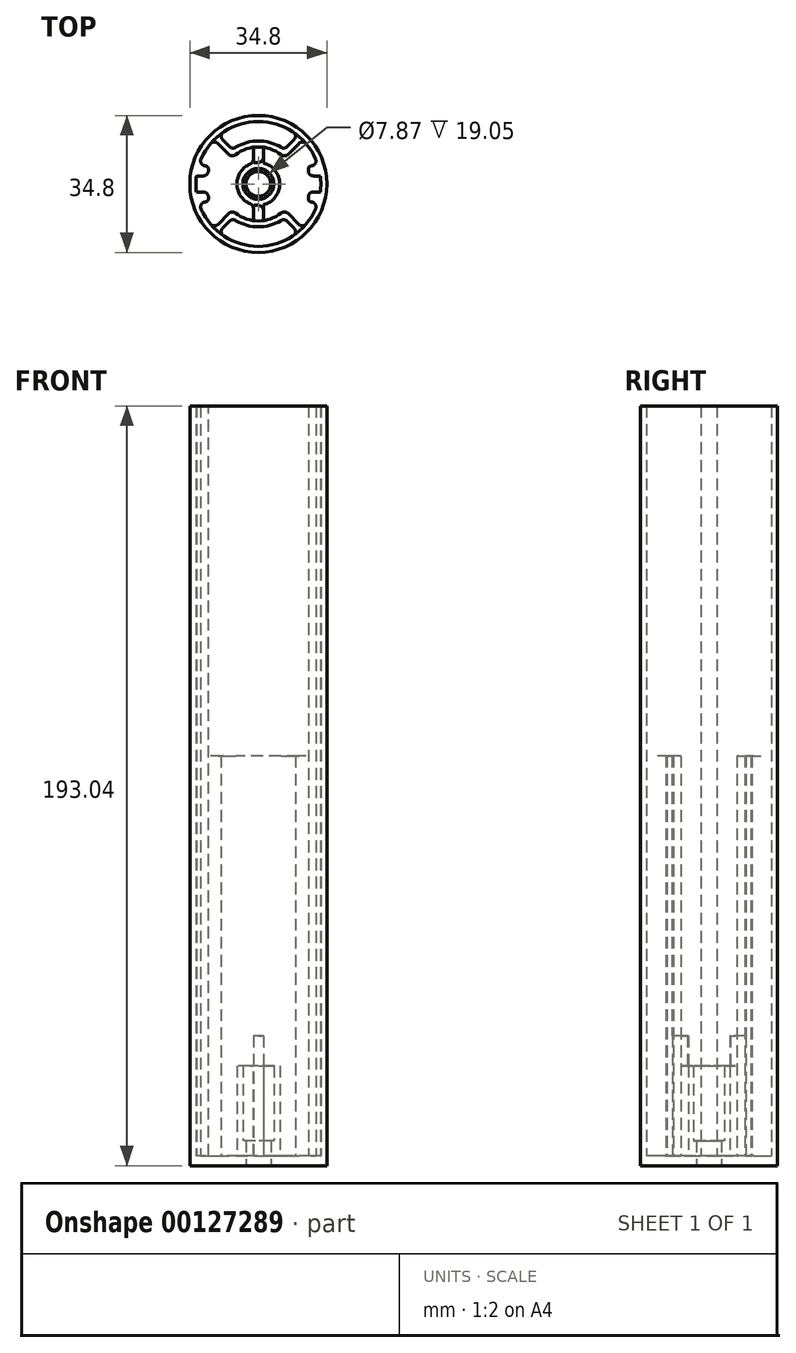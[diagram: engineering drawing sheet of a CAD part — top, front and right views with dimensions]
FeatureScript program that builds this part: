
annotation { "Feature Type Name" : "Feature", "Feature Type Description" : "" }
export const myFeature = defineFeature(function(context is Context, id is Id, definition is map)
    precondition{}
    {
        {
            var Q0;
            Q0=qCreatedBy(makeId("Top.planeOp"),FACE);
            var sketch = newSketch(context, id + "F0", { "sketchPlane" : qUnion([Q0])});
            skCircle(sketch, "E0", {"center": v(0, 0) * mm, "radius": 15.88 * mm, "construction": true});
            skCircle(sketch, "E1", {"center": v(0, 0) * mm, "radius": 17.4 * mm});
            skLineSegment(sketch, "E2", {"start": v(15.88, 0) * mm, "end": v(17.4, 0) * mm, "construction": true});
            skCircle(sketch, "E3", {"center": v(0, 0) * mm, "radius": 3.18 * mm});
            skCircle(sketch, "E4", {"center": v(0, 0) * mm, "radius": 3.94 * mm, "construction": true});
            skCircle(sketch, "E5", {"center": v(0, 0) * mm, "radius": 9.4 * mm, "construction": true});
            skSolve(sketch);
        }
        {
            var Q0;
            Q0 = qSketchRegion(id + "F0", true);
            extrude(context, id + "F1", {"entities" : qUnion([Q0]), "depth" : 2.54 * mm});
        }
        {
            var Q0;
            Q0=makeQuery(id+"F1.opExtrude","CAP_FACE",FACE,{"disambiguationData":[OSD([sQuery(id+"F0.wireOp",EDGE,"E1"),sQuery(id+"F0.wireOp",EDGE,"E3")])],"isStart":false});
            var sketch = newSketch(context, id + "F2", { "sketchPlane" : qUnion([Q0])});
            skCircle(sketch, "E6", {"center": v(0, 0) * mm, "radius": 3.18 * mm});
            skCircle(sketch, "E7", {"center": v(0, 0) * mm, "radius": 5.46 * mm});
            skLineSegment(sketch, "E8", {"start": v(3.94, 0) * mm, "end": v(5.46, 0) * mm});
            skSolve(sketch);
        }
        {
            var Q0;
            Q0 = qSketchRegion(id + "F2", true);
            extrude(context, id + "F3", {"entities" : qUnion([Q0]), "operationType" : NewBodyOperationType.ADD, "depth" : 3.8 * mm});
        }
        {
            var Q0;
            Q0=makeQuery(id+"F3.opExtrude","CAP_FACE",FACE,{"disambiguationData":[OSD([sQuery(id+"F2.wireOp",EDGE,"E6"),sQuery(id+"F2.wireOp",EDGE,"E7")])],"isStart":false});
            var sketch = newSketch(context, id + "F4", { "sketchPlane" : qUnion([Q0])});
            skCircle(sketch, "E9", {"center": v(0, 0) * mm, "radius": 5.46 * mm});
            skCircle(sketch, "E10", {"center": v(0, 0) * mm, "radius": 3.94 * mm});
            skSolve(sketch);
        }
        {
            var Q0;
            Q0 = qSketchRegion(id + "F4", true);
            extrude(context, id + "F5", {"entities" : qUnion([Q0]), "operationType" : NewBodyOperationType.ADD, "depth" : 19.05 * mm});
        }
        {
            var Q0;
            Q0=makeQuery(id+"F1.opExtrude","CAP_FACE",FACE,{"disambiguationData":[OSD([sQuery(id+"F0.wireOp",EDGE,"E1"),sQuery(id+"F0.wireOp",EDGE,"E3")])],"isStart":false});
            var sketch = newSketch(context, id + "F6", { "sketchPlane" : qUnion([Q0])});
            skCircle(sketch, "E11", {"center": v(0, 0) * mm, "radius": 17.4 * mm});
            skLineSegment(sketch, "E12", {"start": v(-11.23, 11.23) * mm, "end": v(-6.65, 6.65) * mm});
            skLineSegment(sketch, "E13", {"start": v(-11.23, -11.23) * mm, "end": v(-6.65, -6.65) * mm});
            skArc(sketch, "E14", {"start": v(-6.65, 6.65) * mm, "mid": v(-9.4, 0) * mm, "end": v(-6.65, -6.65) * mm, "construction": true});
            skArc(sketch, "E15", {"start": v(-6.65, -6.65) * mm, "mid": v(0, -9.4) * mm, "end": v(6.65, -6.65) * mm});
            skArc(sketch, "E16", {"start": v(6.65, -6.65) * mm, "mid": v(9.4, 0) * mm, "end": v(6.65, 6.65) * mm, "construction": true});
            skArc(sketch, "E17", {"start": v(6.65, 6.65) * mm, "mid": v(0, 9.4) * mm, "end": v(-6.65, 6.65) * mm});
            skLineSegment(sketch, "E18", {"start": v(6.65, 6.65) * mm, "end": v(11.23, 11.23) * mm});
            skLineSegment(sketch, "E19", {"start": v(6.65, -6.65) * mm, "end": v(11.23, -11.23) * mm});
            skLineSegment(sketch, "E20", {"start": v(-6.65, -6.65) * mm, "end": v(6.65, 6.65) * mm, "construction": true});
            skLineSegment(sketch, "E21", {"start": v(-6.65, 6.65) * mm, "end": v(6.65, -6.65) * mm, "construction": true});
            skLineSegment(sketch, "E22", {"start": v(-10.1, -12.25) * mm, "end": v(-6.57, -8.72) * mm});
            skLineSegment(sketch, "E23", {"start": v(6.57, -8.72) * mm, "end": v(10.1, -12.25) * mm});
            skArc(sketch, "E24", {"start": v(-6.57, -8.72) * mm, "mid": v(0, -10.92) * mm, "end": v(6.57, -8.72) * mm});
            skArc(sketch, "E25", {"start": v(-10.1, -12.25) * mm, "mid": v(0, -15.87) * mm, "end": v(10.1, -12.25) * mm});
            skArc(sketch, "E26", {"start": v(10.1, -12.25) * mm, "mid": v(10.67, -11.75) * mm, "end": v(11.23, -11.23) * mm, "construction": true});
            skArc(sketch, "E27", {"start": v(-11.23, -11.23) * mm, "mid": v(-10.67, -11.75) * mm, "end": v(-10.1, -12.25) * mm, "construction": true});
            skArc(sketch, "E28", {"start": v(11.23, -11.23) * mm, "mid": v(13.63, -8.15) * mm, "end": v(15.2, -4.57) * mm});
            skLineSegment(sketch, "E29", {"start": v(0, -9.4) * mm, "end": v(0, -10.92) * mm, "construction": true});
            skLineSegment(sketch, "E30", {"start": v(-10.1, 12.25) * mm, "end": v(-6.57, 8.72) * mm});
            skLineSegment(sketch, "E31", {"start": v(10.1, 12.25) * mm, "end": v(6.57, 8.72) * mm});
            skArc(sketch, "E32", {"start": v(6.57, 8.72) * mm, "mid": v(0, 10.92) * mm, "end": v(-6.57, 8.72) * mm});
            skLineSegment(sketch, "E33", {"start": v(0, 9.4) * mm, "end": v(0, 10.92) * mm, "construction": true});
            skArc(sketch, "E34", {"start": v(-11.23, 11.23) * mm, "mid": v(-13.63, 8.15) * mm, "end": v(-15.2, 4.57) * mm});
            skArc(sketch, "E35", {"start": v(-10.1, 12.25) * mm, "mid": v(-10.67, 11.75) * mm, "end": v(-11.23, 11.23) * mm, "construction": true});
            skArc(sketch, "E36", {"start": v(10.1, 12.25) * mm, "mid": v(0, 15.88) * mm, "end": v(-10.1, 12.25) * mm});
            skArc(sketch, "E37", {"start": v(11.23, 11.23) * mm, "mid": v(10.67, 11.75) * mm, "end": v(10.1, 12.25) * mm, "construction": true});
            skArc(sketch, "E38", {"start": v(-15.2, 4.57) * mm, "mid": v(-15.53, 3.31) * mm, "end": v(-15.74, 2.03) * mm, "construction": true});
            skArc(sketch, "E39", {"start": v(-15.74, -2.03) * mm, "mid": v(-15.53, -3.31) * mm, "end": v(-15.2, -4.57) * mm, "construction": true});
            skArc(sketch, "E40", {"start": v(-15.74, 2.03) * mm, "mid": v(-15.88, 0) * mm, "end": v(-15.74, -2.03) * mm});
            skArc(sketch, "E41", {"start": v(-15.2, -4.57) * mm, "mid": v(-13.63, -8.15) * mm, "end": v(-11.23, -11.23) * mm});
            skArc(sketch, "E42", {"start": v(15.2, -4.57) * mm, "mid": v(15.53, -3.31) * mm, "end": v(15.74, -2.03) * mm, "construction": true});
            skArc(sketch, "E43", {"start": v(15.74, -2.03) * mm, "mid": v(15.88, 0) * mm, "end": v(15.74, 2.03) * mm});
            skArc(sketch, "E44", {"start": v(15.74, 2.03) * mm, "mid": v(15.53, 3.31) * mm, "end": v(15.2, 4.57) * mm, "construction": true});
            skArc(sketch, "E45", {"start": v(15.2, 4.57) * mm, "mid": v(13.63, 8.15) * mm, "end": v(11.23, 11.23) * mm});
            skPoint(sketch, "E46", {"position": v(-15.88, 0) * mm});
            skPoint(sketch, "E47", {"position": v(15.88, 0) * mm});
            skLineSegment(sketch, "E48", {"start": v(-15.2, 4.57) * mm, "end": v(-12.7, 4.57) * mm});
            skLineSegment(sketch, "E49", {"start": v(-12.7, 4.57) * mm, "end": v(-12.7, 2.03) * mm});
            skLineSegment(sketch, "E50", {"start": v(-12.7, 2.03) * mm, "end": v(-15.74, 2.03) * mm});
            skLineSegment(sketch, "E51", {"start": v(-15.74, -2.03) * mm, "end": v(-12.7, -2.03) * mm});
            skLineSegment(sketch, "E52", {"start": v(-12.7, -2.03) * mm, "end": v(-12.7, -4.57) * mm});
            skLineSegment(sketch, "E53", {"start": v(-12.7, -4.57) * mm, "end": v(-15.2, -4.57) * mm});
            skLineSegment(sketch, "E54", {"start": v(15.2, 4.57) * mm, "end": v(12.7, 4.57) * mm});
            skLineSegment(sketch, "E55", {"start": v(12.7, 4.57) * mm, "end": v(12.7, 2.03) * mm});
            skLineSegment(sketch, "E56", {"start": v(12.7, 2.03) * mm, "end": v(15.74, 2.03) * mm});
            skLineSegment(sketch, "E57", {"start": v(15.74, -2.03) * mm, "end": v(12.7, -2.03) * mm});
            skLineSegment(sketch, "E58", {"start": v(12.7, -2.03) * mm, "end": v(12.7, -4.57) * mm});
            skLineSegment(sketch, "E59", {"start": v(12.7, -4.57) * mm, "end": v(15.2, -4.57) * mm});
            skSolve(sketch);
        }
        {
            var Q0;
            Q0 = qSketchRegion(id + "F6", true);
            extrude(context, id + "F7", {"entities" : qUnion([Q0]), "operationType" : NewBodyOperationType.ADD, "depth" : 101.6 * mm});
        }
        {
            var Q0;
            Q0=makeQuery(id+"F7.boolean.opBoolean","SPLIT",FACE,{"disambiguationData":[TD([makeQuery(id+"F3.opExtrude","SWEPT_FACE",FACE,{"disambiguationData":[OSD([sQuery(id+"F2.wireOp",EDGE,"E7")])]})])],"derivedFrom":makeQuery(id+"F1.opExtrude","CAP_FACE",FACE,{"disambiguationData":[OSD([sQuery(id+"F0.wireOp",EDGE,"E1"),sQuery(id+"F0.wireOp",EDGE,"E3")])],"isStart":false})});
            var sketch = newSketch(context, id + "F8", { "sketchPlane" : qUnion([Q0])});
            skLineSegment(sketch, "E60", {"start": v(-1.27, 9.31) * mm, "end": v(-1.27, 5.31) * mm});
            skLineSegment(sketch, "E61", {"start": v(1.27, 9.31) * mm, "end": v(1.27, 5.31) * mm});
            skArc(sketch, "E62", {"start": v(1.27, 5.31) * mm, "mid": v(0, 5.46) * mm, "end": v(-1.27, 5.31) * mm});
            skArc(sketch, "E63", {"start": v(1.27, 9.31) * mm, "mid": v(0, 9.4) * mm, "end": v(-1.27, 9.31) * mm});
            skLineSegment(sketch, "E64", {"start": v(-1.27, -5.31) * mm, "end": v(-1.27, -9.31) * mm});
            skLineSegment(sketch, "E65", {"start": v(1.27, -5.31) * mm, "end": v(1.27, -9.31) * mm});
            skArc(sketch, "E66", {"start": v(-1.27, -5.31) * mm, "mid": v(0, -5.46) * mm, "end": v(1.27, -5.31) * mm});
            skArc(sketch, "E67", {"start": v(-1.27, -9.31) * mm, "mid": v(0, -9.4) * mm, "end": v(1.27, -9.31) * mm});
            skSolve(sketch);
        }
        {
            var Q0;
            Q0 = qSketchRegion(id + "F8", true);
            extrude(context, id + "F9", {"entities" : qUnion([Q0]), "operationType" : NewBodyOperationType.ADD, "depth" : 30.48 * mm});
        }
        {
            var Q0;
            Q0=makeQuery(id+"F7.opExtrude","CAP_FACE",FACE,{"disambiguationData":[OSD([sQuery(id+"F6.wireOp",EDGE,"E11"),sQuery(id+"F6.wireOp",EDGE,"E12"),sQuery(id+"F6.wireOp",EDGE,"E13"),sQuery(id+"F6.wireOp",EDGE,"E15"),sQuery(id+"F6.wireOp",EDGE,"E17"),sQuery(id+"F6.wireOp",EDGE,"E18"),sQuery(id+"F6.wireOp",EDGE,"E19"),sQuery(id+"F6.wireOp",EDGE,"E22"),sQuery(id+"F6.wireOp",EDGE,"E23"),sQuery(id+"F6.wireOp",EDGE,"E24"),sQuery(id+"F6.wireOp",EDGE,"E25"),sQuery(id+"F6.wireOp",EDGE,"E28"),sQuery(id+"F6.wireOp",EDGE,"E30"),sQuery(id+"F6.wireOp",EDGE,"E31"),sQuery(id+"F6.wireOp",EDGE,"E32"),sQuery(id+"F6.wireOp",EDGE,"E34"),sQuery(id+"F6.wireOp",EDGE,"E36"),sQuery(id+"F6.wireOp",EDGE,"E40"),sQuery(id+"F6.wireOp",EDGE,"E41"),sQuery(id+"F6.wireOp",EDGE,"E43"),sQuery(id+"F6.wireOp",EDGE,"E45"),sQuery(id+"F6.wireOp",EDGE,"E48"),sQuery(id+"F6.wireOp",EDGE,"E49"),sQuery(id+"F6.wireOp",EDGE,"E50"),sQuery(id+"F6.wireOp",EDGE,"E51"),sQuery(id+"F6.wireOp",EDGE,"E52"),sQuery(id+"F6.wireOp",EDGE,"E53"),sQuery(id+"F6.wireOp",EDGE,"E54"),sQuery(id+"F6.wireOp",EDGE,"E55"),sQuery(id+"F6.wireOp",EDGE,"E56"),sQuery(id+"F6.wireOp",EDGE,"E57"),sQuery(id+"F6.wireOp",EDGE,"E58"),sQuery(id+"F6.wireOp",EDGE,"E59")])],"isStart":false});
            var sketch = newSketch(context, id + "F10", { "sketchPlane" : qUnion([Q0])});
            skCircle(sketch, "E68", {"center": v(0, 0) * mm, "radius": 17.4 * mm});
            skArc(sketch, "E69", {"start": v(15.2, 4.57) * mm, "mid": v(0, 15.88) * mm, "end": v(-15.2, 4.57) * mm});
            skArc(sketch, "E70", {"start": v(-15.2, -4.57) * mm, "mid": v(0, -15.88) * mm, "end": v(15.2, -4.57) * mm});
            skLineSegment(sketch, "E71", {"start": v(-15.2, 4.57) * mm, "end": v(-12.7, 4.57) * mm});
            skLineSegment(sketch, "E72", {"start": v(-12.7, 4.57) * mm, "end": v(-12.7, 2.03) * mm});
            skLineSegment(sketch, "E73", {"start": v(-12.7, 2.03) * mm, "end": v(-15.74, 2.03) * mm});
            skLineSegment(sketch, "E74", {"start": v(-15.74, -2.03) * mm, "end": v(-12.7, -2.03) * mm});
            skLineSegment(sketch, "E75", {"start": v(-12.7, -2.03) * mm, "end": v(-12.7, -4.57) * mm});
            skLineSegment(sketch, "E76", {"start": v(-12.7, -4.57) * mm, "end": v(-15.2, -4.57) * mm});
            skLineSegment(sketch, "E77", {"start": v(15.74, -2.03) * mm, "end": v(12.7, -2.03) * mm});
            skLineSegment(sketch, "E78", {"start": v(12.7, -2.03) * mm, "end": v(12.7, -4.57) * mm});
            skLineSegment(sketch, "E79", {"start": v(12.7, -4.57) * mm, "end": v(15.2, -4.57) * mm});
            skLineSegment(sketch, "E80", {"start": v(15.74, 2.03) * mm, "end": v(12.7, 2.03) * mm});
            skLineSegment(sketch, "E81", {"start": v(12.7, 2.03) * mm, "end": v(12.7, 4.57) * mm});
            skLineSegment(sketch, "E82", {"start": v(12.7, 4.57) * mm, "end": v(15.2, 4.57) * mm});
            skArc(sketch, "E83", {"start": v(-15.74, 2.03) * mm, "mid": v(-15.88, 0) * mm, "end": v(-15.74, -2.03) * mm});
            skArc(sketch, "E84", {"start": v(15.74, -2.03) * mm, "mid": v(15.88, 0) * mm, "end": v(15.74, 2.03) * mm});
            skSolve(sketch);
        }
        {
            var Q0;
            Q0 = qSketchRegion(id + "F10", true);
            extrude(context, id + "F11", {"entities" : qUnion([Q0]), "operationType" : NewBodyOperationType.ADD, "depth" : 88.9 * mm});
        }
        {
            var Q0;
            Q0=makeQuery(id+"F7.opExtrude","SWEPT_EDGE",EDGE,{"disambiguationData":[OSD([sQuery(id+"F6.wireOp",EDGE,"E13"),sQuery(id+"F6.wireOp",EDGE,"E15")])]});
            var Q1;
            Q1=makeQuery(id+"F7.opExtrude","SWEPT_EDGE",EDGE,{"disambiguationData":[OSD([sQuery(id+"F6.wireOp",EDGE,"E15"),sQuery(id+"F6.wireOp",EDGE,"E19")])]});
            var Q2;
            Q2=makeQuery(id+"F7.opExtrude","SWEPT_EDGE",EDGE,{"disambiguationData":[OSD([sQuery(id+"F6.wireOp",EDGE,"E19"),sQuery(id+"F6.wireOp",EDGE,"E28")])]});
            var Q3;
            Q3=makeQuery(id+"F7.opExtrude","SWEPT_EDGE",EDGE,{"disambiguationData":[OSD([sQuery(id+"F6.wireOp",EDGE,"E13"),sQuery(id+"F6.wireOp",EDGE,"E34")])]});
            var Q4;
            Q4=makeQuery(id+"F7.opExtrude","SWEPT_EDGE",EDGE,{"disambiguationData":[OSD([sQuery(id+"F6.wireOp",EDGE,"E22"),sQuery(id+"F6.wireOp",EDGE,"E24")])]});
            var Q5;
            Q5=makeQuery(id+"F7.opExtrude","SWEPT_EDGE",EDGE,{"disambiguationData":[OSD([sQuery(id+"F6.wireOp",EDGE,"E23"),sQuery(id+"F6.wireOp",EDGE,"E24")])]});
            var Q6;
            Q6=makeQuery(id+"F7.opExtrude","SWEPT_EDGE",EDGE,{"disambiguationData":[OSD([sQuery(id+"F6.wireOp",EDGE,"E23"),sQuery(id+"F6.wireOp",EDGE,"E25")])]});
            var Q7;
            Q7=makeQuery(id+"F7.opExtrude","SWEPT_EDGE",EDGE,{"disambiguationData":[OSD([sQuery(id+"F6.wireOp",EDGE,"E22"),sQuery(id+"F6.wireOp",EDGE,"E25")])]});
            var Q8;
            Q8=makeQuery(id+"F7.opExtrude","SWEPT_EDGE",EDGE,{"disambiguationData":[OSD([sQuery(id+"F6.wireOp",EDGE,"E12"),sQuery(id+"F6.wireOp",EDGE,"E17")])]});
            var Q9;
            Q9=makeQuery(id+"F7.opExtrude","SWEPT_EDGE",EDGE,{"disambiguationData":[OSD([sQuery(id+"F6.wireOp",EDGE,"E30"),sQuery(id+"F6.wireOp",EDGE,"E36")])]});
            var Q10;
            Q10=makeQuery(id+"F7.opExtrude","SWEPT_EDGE",EDGE,{"disambiguationData":[OSD([sQuery(id+"F6.wireOp",EDGE,"E17"),sQuery(id+"F6.wireOp",EDGE,"E18")])]});
            var Q11;
            Q11=makeQuery(id+"F7.opExtrude","SWEPT_EDGE",EDGE,{"disambiguationData":[OSD([sQuery(id+"F6.wireOp",EDGE,"E18"),sQuery(id+"F6.wireOp",EDGE,"E28")])]});
            var Q12;
            Q12=makeQuery(id+"F7.opExtrude","SWEPT_EDGE",EDGE,{"disambiguationData":[OSD([sQuery(id+"F6.wireOp",EDGE,"E31"),sQuery(id+"F6.wireOp",EDGE,"E36")])]});
            var Q13;
            Q13=makeQuery(id+"F7.opExtrude","SWEPT_EDGE",EDGE,{"disambiguationData":[OSD([sQuery(id+"F6.wireOp",EDGE,"E31"),sQuery(id+"F6.wireOp",EDGE,"E32")])]});
            var Q14;
            Q14=makeQuery(id+"F7.opExtrude","SWEPT_EDGE",EDGE,{"disambiguationData":[OSD([sQuery(id+"F6.wireOp",EDGE,"E12"),sQuery(id+"F6.wireOp",EDGE,"E34")])]});
            var Q15;
            Q15=makeQuery(id+"F7.opExtrude","SWEPT_EDGE",EDGE,{"disambiguationData":[OSD([sQuery(id+"F6.wireOp",EDGE,"E30"),sQuery(id+"F6.wireOp",EDGE,"E32")])]});
            var Q16;
            Q16=makeQuery(id+"F9.opExtrude","SWEPT_EDGE",EDGE,{"disambiguationData":[OSD([sQuery(id+"F6.wireOp",EDGE,"E17"),sQuery(id+"F8.wireOp",EDGE,"E61"),sQuery(id+"F8.wireOp",EDGE,"E63")])]});
            var Q17;
            {var subQ0=sQuery(id+"F2.wireOp",EDGE,"E7");var subQ1=sQuery(id+"F8.wireOp",EDGE,"E61");Q17=makeQuery(id+"F9.boolean.opBoolean","SPLIT",EDGE,{"disambiguationData":[topologyDisambiguationEdgeConnected([makeQuery(id+"F3.opExtrude","SWEPT_FACE",FACE,{"disambiguationData":[OSD([subQ0])]})])],"derivedFrom":makeQuery(id+"F9.opExtrude","SWEPT_EDGE",EDGE,{"disambiguationData":[OSD([subQ0,subQ1,sQuery(id+"F8.wireOp",EDGE,"E62")])]})});}
            var Q18;
            {var subQ0=sQuery(id+"F2.wireOp",EDGE,"E7");var subQ1=sQuery(id+"F8.wireOp",EDGE,"E65");Q18=makeQuery(id+"F9.boolean.opBoolean","SPLIT",EDGE,{"disambiguationData":[topologyDisambiguationEdgeConnected([makeQuery(id+"F3.opExtrude","SWEPT_FACE",FACE,{"disambiguationData":[OSD([subQ0])]})])],"derivedFrom":makeQuery(id+"F9.opExtrude","SWEPT_EDGE",EDGE,{"disambiguationData":[OSD([subQ0,subQ1,sQuery(id+"F8.wireOp",EDGE,"E66")])]})});}
            var Q19;
            Q19=makeQuery(id+"F9.opExtrude","SWEPT_EDGE",EDGE,{"disambiguationData":[OSD([sQuery(id+"F6.wireOp",EDGE,"E15"),sQuery(id+"F8.wireOp",EDGE,"E65"),sQuery(id+"F8.wireOp",EDGE,"E67")])]});
            var Q20;
            Q20=makeQuery(id+"F9.opExtrude","SWEPT_EDGE",EDGE,{"disambiguationData":[OSD([sQuery(id+"F6.wireOp",EDGE,"E15"),sQuery(id+"F8.wireOp",EDGE,"E64"),sQuery(id+"F8.wireOp",EDGE,"E67")])]});
            var Q21;
            {var subQ0=sQuery(id+"F2.wireOp",EDGE,"E7");var subQ1=sQuery(id+"F8.wireOp",EDGE,"E60");Q21=makeQuery(id+"F9.boolean.opBoolean","SPLIT",EDGE,{"disambiguationData":[topologyDisambiguationEdgeConnected([makeQuery(id+"F3.opExtrude","SWEPT_FACE",FACE,{"disambiguationData":[OSD([subQ0])]})])],"derivedFrom":makeQuery(id+"F9.opExtrude","SWEPT_EDGE",EDGE,{"disambiguationData":[OSD([subQ0,subQ1,sQuery(id+"F8.wireOp",EDGE,"E62")])]})});}
            var Q22;
            Q22=makeQuery(id+"F9.opExtrude","SWEPT_EDGE",EDGE,{"disambiguationData":[OSD([sQuery(id+"F6.wireOp",EDGE,"E17"),sQuery(id+"F8.wireOp",EDGE,"E60"),sQuery(id+"F8.wireOp",EDGE,"E63")])]});
            var Q23;
            {var subQ0=sQuery(id+"F2.wireOp",EDGE,"E7");var subQ1=sQuery(id+"F8.wireOp",EDGE,"E64");Q23=makeQuery(id+"F9.boolean.opBoolean","SPLIT",EDGE,{"disambiguationData":[topologyDisambiguationEdgeConnected([makeQuery(id+"F3.opExtrude","SWEPT_FACE",FACE,{"disambiguationData":[OSD([subQ0])]})])],"derivedFrom":makeQuery(id+"F9.opExtrude","SWEPT_EDGE",EDGE,{"disambiguationData":[OSD([subQ0,subQ1,sQuery(id+"F8.wireOp",EDGE,"E66")])]})});}
            var Q24;
            Q24=makeQuery(id+"F9.opExtrude","CAP_EDGE",EDGE,{"disambiguationData":[OSD([sQuery(id+"F8.wireOp",EDGE,"E63")])],"isStart":false});
            var Q25;
            Q25=makeQuery(id+"F9.opExtrude","CAP_EDGE",EDGE,{"disambiguationData":[OSD([sQuery(id+"F8.wireOp",EDGE,"E67")])],"isStart":false});
            var Q26;
            Q26=makeQuery(id+"F7.opExtrude","SWEPT_EDGE",EDGE,{"disambiguationData":[OSD([sQuery(id+"F6.wireOp",EDGE,"E49"),sQuery(id+"F6.wireOp",EDGE,"E50")])]});
            var Q27;
            Q27=makeQuery(id+"F7.opExtrude","SWEPT_EDGE",EDGE,{"disambiguationData":[OSD([sQuery(id+"F6.wireOp",EDGE,"E51"),sQuery(id+"F6.wireOp",EDGE,"E52")])]});
            var Q28;
            Q28=makeQuery(id+"F7.opExtrude","SWEPT_EDGE",EDGE,{"disambiguationData":[OSD([sQuery(id+"F6.wireOp",EDGE,"E41"),sQuery(id+"F6.wireOp",EDGE,"E53")])]});
            var Q29;
            Q29=makeQuery(id+"F7.opExtrude","SWEPT_EDGE",EDGE,{"disambiguationData":[OSD([sQuery(id+"F6.wireOp",EDGE,"E55"),sQuery(id+"F6.wireOp",EDGE,"E56")])]});
            var Q30;
            Q30=makeQuery(id+"F7.opExtrude","SWEPT_EDGE",EDGE,{"disambiguationData":[OSD([sQuery(id+"F6.wireOp",EDGE,"E57"),sQuery(id+"F6.wireOp",EDGE,"E58")])]});
            var Q31;
            Q31=makeQuery(id+"F7.opExtrude","SWEPT_EDGE",EDGE,{"disambiguationData":[OSD([sQuery(id+"F6.wireOp",EDGE,"E45"),sQuery(id+"F6.wireOp",EDGE,"E54")])]});
            fillet(context, id + "F12", {"entities" : qUnion([Q0, Q1, Q2, Q3, Q4, Q5, Q6, Q7, Q8, Q9, Q10, Q11, Q12, Q13, Q14, Q15, Q16, Q17, Q18, Q19, Q20, Q21, Q22, Q23, Q24, Q25, Q26, Q27, Q28, Q29, Q30, Q31]), "radius" : 1.27 * mm, "tangentPropagation" : true, "allowEdgeOverflow" : false});
        }
        {
            var Q0;
            Q0=makeQuery(id+"F7.opExtrude","SWEPT_EDGE",EDGE,{"disambiguationData":[OSD([sQuery(id+"F6.wireOp",EDGE,"E52"),sQuery(id+"F6.wireOp",EDGE,"E53")])]});
            var Q1;
            Q1=makeQuery(id+"F7.opExtrude","SWEPT_EDGE",EDGE,{"disambiguationData":[OSD([sQuery(id+"F6.wireOp",EDGE,"E48"),sQuery(id+"F6.wireOp",EDGE,"E49")])]});
            var Q2;
            Q2=makeQuery(id+"F7.opExtrude","SWEPT_EDGE",EDGE,{"disambiguationData":[OSD([sQuery(id+"F6.wireOp",EDGE,"E54"),sQuery(id+"F6.wireOp",EDGE,"E55")])]});
            var Q3;
            Q3=makeQuery(id+"F7.opExtrude","SWEPT_EDGE",EDGE,{"disambiguationData":[OSD([sQuery(id+"F6.wireOp",EDGE,"E58"),sQuery(id+"F6.wireOp",EDGE,"E59")])]});
            fillet(context, id + "F13", {"entities" : qUnion([Q0, Q1, Q2, Q3]), "radius" : 0.76 * mm, "tangentPropagation" : true, "allowEdgeOverflow" : false});
        }
    });
